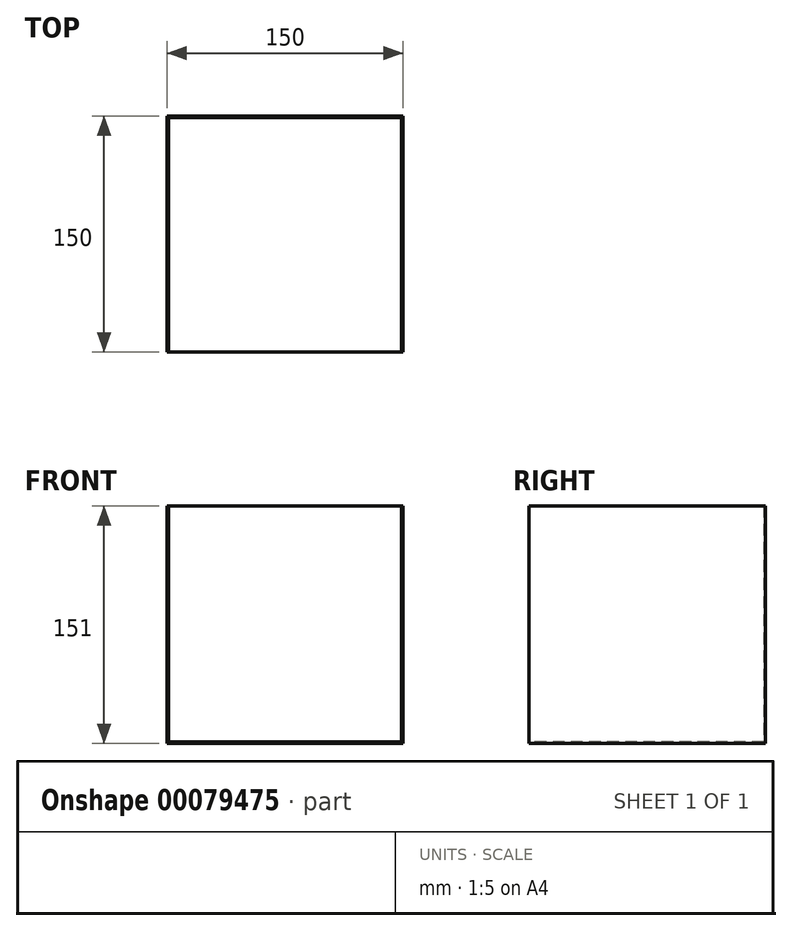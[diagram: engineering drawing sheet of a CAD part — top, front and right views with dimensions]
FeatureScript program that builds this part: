
annotation { "Feature Type Name" : "Feature", "Feature Type Description" : "" }
export const myFeature = defineFeature(function(context is Context, id is Id, definition is map)
    precondition{}
    {
        {
            var Q0;
            Q0=qCreatedBy(makeId("Top.planeOp"),FACE);
            var sketch = newSketch(context, id + "F0", { "sketchPlane" : qUnion([Q0])});
            skLineSegment(sketch, "E0.bottom", {"start": v(75, 75) * mm, "end": v(-75, 75) * mm});
            skLineSegment(sketch, "E0.top", {"start": v(75, -75) * mm, "end": v(-75, -75) * mm});
            skLineSegment(sketch, "E0.left", {"start": v(75, 75) * mm, "end": v(75, -75) * mm});
            skLineSegment(sketch, "E0.right", {"start": v(-75, 75) * mm, "end": v(-75, -75) * mm});
            skPoint(sketch, "E0.middle", {"position": v(0, 0) * mm});
            skSolve(sketch);
        }
        {
            var Q0;
            Q0=makeQuery(id+"F0.imprint","IMPRINT",FACE,{"disambiguationData":[TD([[makeQuery(id+"F0.imprint","IMPRINT",EDGE,{"derivedFrom":sQuery(id+"F0.wireOp",EDGE,"E0.bottom")}),1.0]])]});
            extrude(context, id + "F1", {"entities" : qUnion([Q0]), "depth" : 1 * mm, "offsetDistance" : 25 * mm});
        }
        {
            var Q0;
            Q0=makeQuery(id+"F1.opExtrude","CAP_FACE",FACE,{"disambiguationData":[OSD([sQuery(id+"F0.wireOp",EDGE,"E0.bottom"),sQuery(id+"F0.wireOp",EDGE,"E0.top"),sQuery(id+"F0.wireOp",EDGE,"E0.left"),sQuery(id+"F0.wireOp",EDGE,"E0.right")])],"isStart":false});
            var sketch = newSketch(context, id + "F2", { "sketchPlane" : qUnion([Q0])});
            skLineSegment(sketch, "E1.0", {"start": v(75, 75) * mm, "end": v(75, -75) * mm});
            skLineSegment(sketch, "E2.0", {"start": v(75, 75) * mm, "end": v(-75, 75) * mm});
            skLineSegment(sketch, "E3.0", {"start": v(-75, 75) * mm, "end": v(-75, -75) * mm});
            skLineSegment(sketch, "E4.0", {"start": v(74, 74) * mm, "end": v(74, -75) * mm});
            skLineSegment(sketch, "E5.0", {"start": v(-74, 74) * mm, "end": v(-74, -75) * mm});
            skLineSegment(sketch, "E5.1", {"start": v(74, 74) * mm, "end": v(-74, 74) * mm});
            skLineSegment(sketch, "E6", {"start": v(-75, -75) * mm, "end": v(-74, -75) * mm});
            skLineSegment(sketch, "E7", {"start": v(74, -75) * mm, "end": v(75, -75) * mm});
            skSolve(sketch);
        }
        {
            var Q0;
            Q0 = qSketchRegion(id + "F2", true);
            extrude(context, id + "F3", {"entities" : qUnion([Q0]), "operationType" : NewBodyOperationType.ADD, "depth" : 150 * mm, "offsetDistance" : 25 * mm});
        }
    });
